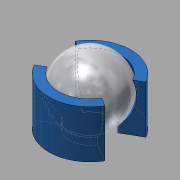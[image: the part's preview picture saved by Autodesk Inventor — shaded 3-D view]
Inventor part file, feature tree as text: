
AUTODESK INVENTOR PART (.ipt)
format: ipt  version: 2015 (Build 190159000, 159)  size: 154,624 bytes
history: native  units: mm
features: sketch x3, revolve x2, extrude x1, boolean_combine x1
ambient origin geometry x8: Origin, YZ Plane, XZ Plane, XY Plane, X Axis, Y Axis, Z Axis, Center Point
bodies: Solid2 (feature_tree), Solid3 (feature_tree), Solid1 (feature_tree)
feature tree (7):
  extrude  "Extrusion1"  Depth=3.0mm
  revolve  "Revolution1"  [1 undecoded]
  boolean_combine  "Combine1"
  revolve  "Revolution2"  [1 undecoded]
  sketch  "Sketch1"  dims[d0=6.0mm d1=3.0mm]
  sketch  "Sketch4"  dims[d2=1.0mm d3=2.5mm d4=0.0mm d5=0.0mm d8=2.5mm]
  sketch  "Sketch5"  dims[d9=20.071286mm d10=2.4mm d11=20.071286mm]
note: 2 required parameter values undecoded (feature->parameter linkage not recoverable at this tier; creation-order binding heuristic only, values carry confidence <= 0.55)
